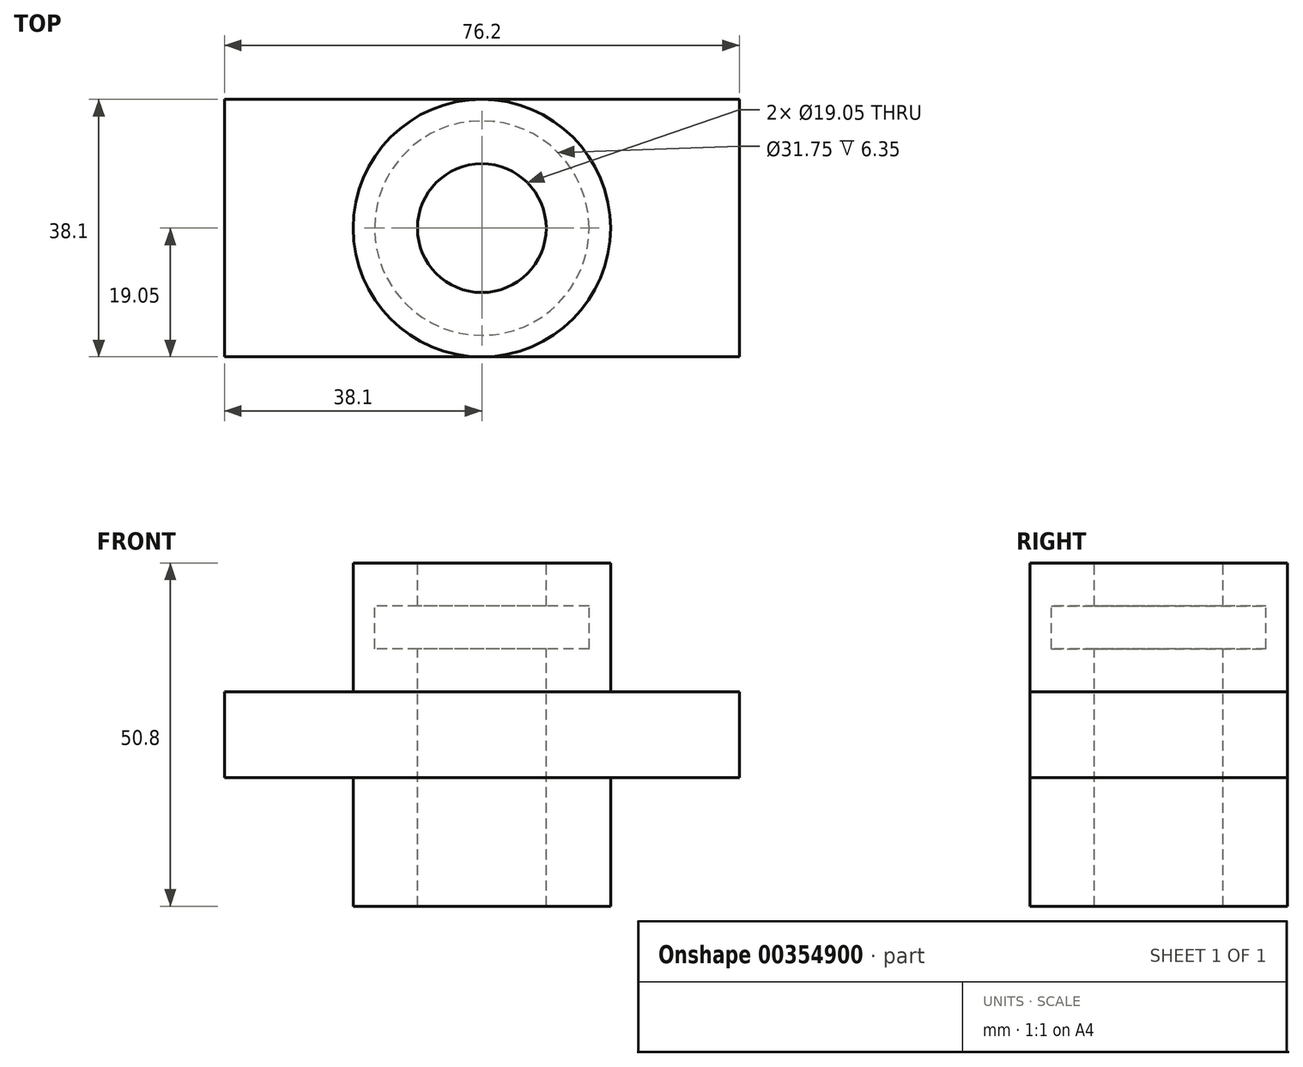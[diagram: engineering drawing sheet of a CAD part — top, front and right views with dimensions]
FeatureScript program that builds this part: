
annotation { "Feature Type Name" : "Feature", "Feature Type Description" : "" }
export const myFeature = defineFeature(function(context is Context, id is Id, definition is map)
    precondition{}
    {
        {
            var Q0;
            Q0=qCreatedBy(makeId("Top.planeOp"),FACE);
            var sketch = newSketch(context, id + "F0", { "sketchPlane" : qUnion([Q0])});
            skCircle(sketch, "E0", {"center": v(0, 0) * mm, "radius": 19.05 * mm});
            skLineSegment(sketch, "E1", {"start": v(0, -19.05) * mm, "end": v(0, 19.05) * mm, "construction": true});
            skLineSegment(sketch, "E2", {"start": v(0, 19.05) * mm, "end": v(38.1, 19.05) * mm});
            skLineSegment(sketch, "E3", {"start": v(38.1, 19.05) * mm, "end": v(38.1, -19.05) * mm});
            skLineSegment(sketch, "E4", {"start": v(38.1, -19.05) * mm, "end": v(0, -19.05) * mm});
            skLineSegment(sketch, "E5", {"start": v(0, 19.05) * mm, "end": v(-38.1, 19.05) * mm});
            skLineSegment(sketch, "E6", {"start": v(-38.1, 19.05) * mm, "end": v(-38.1, -19.05) * mm});
            skLineSegment(sketch, "E7", {"start": v(-38.1, -19.05) * mm, "end": v(0, -19.05) * mm});
            skLineSegment(sketch, "E8", {"start": v(-38.1, 0) * mm, "end": v(38.1, 0) * mm, "construction": true});
            skLineSegment(sketch, "E9", {"start": v(19.05, 0) * mm, "end": v(38.1, 0) * mm, "construction": true});
            skSolve(sketch);
        }
        {
            var Q0;
            Q0=makeQuery(id+"F0.imprint","IMPRINT",FACE,{"disambiguationData":[TD([[makeQuery(id+"F0.imprint","IMPRINT",EDGE,{"derivedFrom":sQuery(id+"F0.wireOp",EDGE,"E0")}),1.0]])]});
            extrude(context, id + "F1", {"entities" : qUnion([Q0]), "endBound" : BoundingType.SYMMETRIC, "depth" : 50.8 * mm});
        }
        {
            var Q0;
            Q0=makeQuery(id+"F1.opExtrude","CAP_FACE",FACE,{"disambiguationData":[OSD([sQuery(id+"F0.wireOp",EDGE,"E0")])],"isStart":false});
            var sketch = newSketch(context, id + "F2", { "sketchPlane" : qUnion([Q0])});
            skCircle(sketch, "E10", {"center": v(0, 0) * mm, "radius": 9.53 * mm});
            skSolve(sketch);
        }
        {
            var Q0;
            Q0=makeQuery(id+"F2.imprint","IMPRINT",FACE,{"disambiguationData":[TD([[makeQuery(id+"F2.imprint","IMPRINT",EDGE,{"derivedFrom":sQuery(id+"F2.wireOp",EDGE,"E10")}),1.0]])]});
            extrude(context, id + "F3", {"entities" : qUnion([Q0]), "operationType" : NewBodyOperationType.REMOVE, "oppositeDirection" : true, "depth" : 6.35 * mm});
        }
        {
            var Q0;
            Q0=makeQuery(id+"F3.boolean.opBoolean","COPY",FACE,{"derivedFrom":makeQuery(id+"F3.opExtrude","CAP_FACE",FACE,{"disambiguationData":[OSD([sQuery(id+"F2.wireOp",EDGE,"E10")])],"isStart":false})});
            var sketch = newSketch(context, id + "F4", { "sketchPlane" : qUnion([Q0])});
            skCircle(sketch, "E11", {"center": v(0, 0) * mm, "radius": 15.88 * mm});
            skSolve(sketch);
        }
        {
            var Q0;
            Q0 = qSketchRegion(id + "F4", true);
            extrude(context, id + "F5", {"entities" : qUnion([Q0]), "operationType" : NewBodyOperationType.REMOVE, "oppositeDirection" : true, "depth" : 6.35 * mm});
        }
        {
            var Q0;
            Q0=makeQuery(id+"F5.boolean.opBoolean","COPY",FACE,{"derivedFrom":makeQuery(id+"F5.opExtrude","CAP_FACE",FACE,{"disambiguationData":[OSD([sQuery(id+"F4.wireOp",EDGE,"E11")])],"isStart":false})});
            var sketch = newSketch(context, id + "F6", { "sketchPlane" : qUnion([Q0])});
            skCircle(sketch, "E12", {"center": v(0, 0) * mm, "radius": 9.53 * mm});
            skSolve(sketch);
        }
        {
            var Q0;
            Q0 = qSketchRegion(id + "F6", true);
            extrude(context, id + "F7", {"entities" : qUnion([Q0]), "operationType" : NewBodyOperationType.REMOVE, "oppositeDirection" : true, "depth" : 76.2 * mm});
        }
        {
            var Q0;
            {var subQ0=sQuery(id+"F0.wireOp",EDGE,"E5");Q0=makeQuery(id+"F0.imprint","IMPRINT",FACE,{"disambiguationData":[TD([[makeQuery(id+"F0.imprint","IMPRINT",EDGE,{"derivedFrom":subQ0}),1.0]])]});}
            var Q1;
            {var subQ0=sQuery(id+"F0.wireOp",EDGE,"E2");Q1=makeQuery(id+"F0.imprint","IMPRINT",FACE,{"disambiguationData":[TD([[makeQuery(id+"F0.imprint","IMPRINT",EDGE,{"derivedFrom":subQ0}),-1.0]])]});}
            extrude(context, id + "F8", {"entities" : qUnion([Q0, Q1]), "operationType" : NewBodyOperationType.ADD, "endBound" : BoundingType.SYMMETRIC, "depth" : 12.7 * mm});
        }
    });
